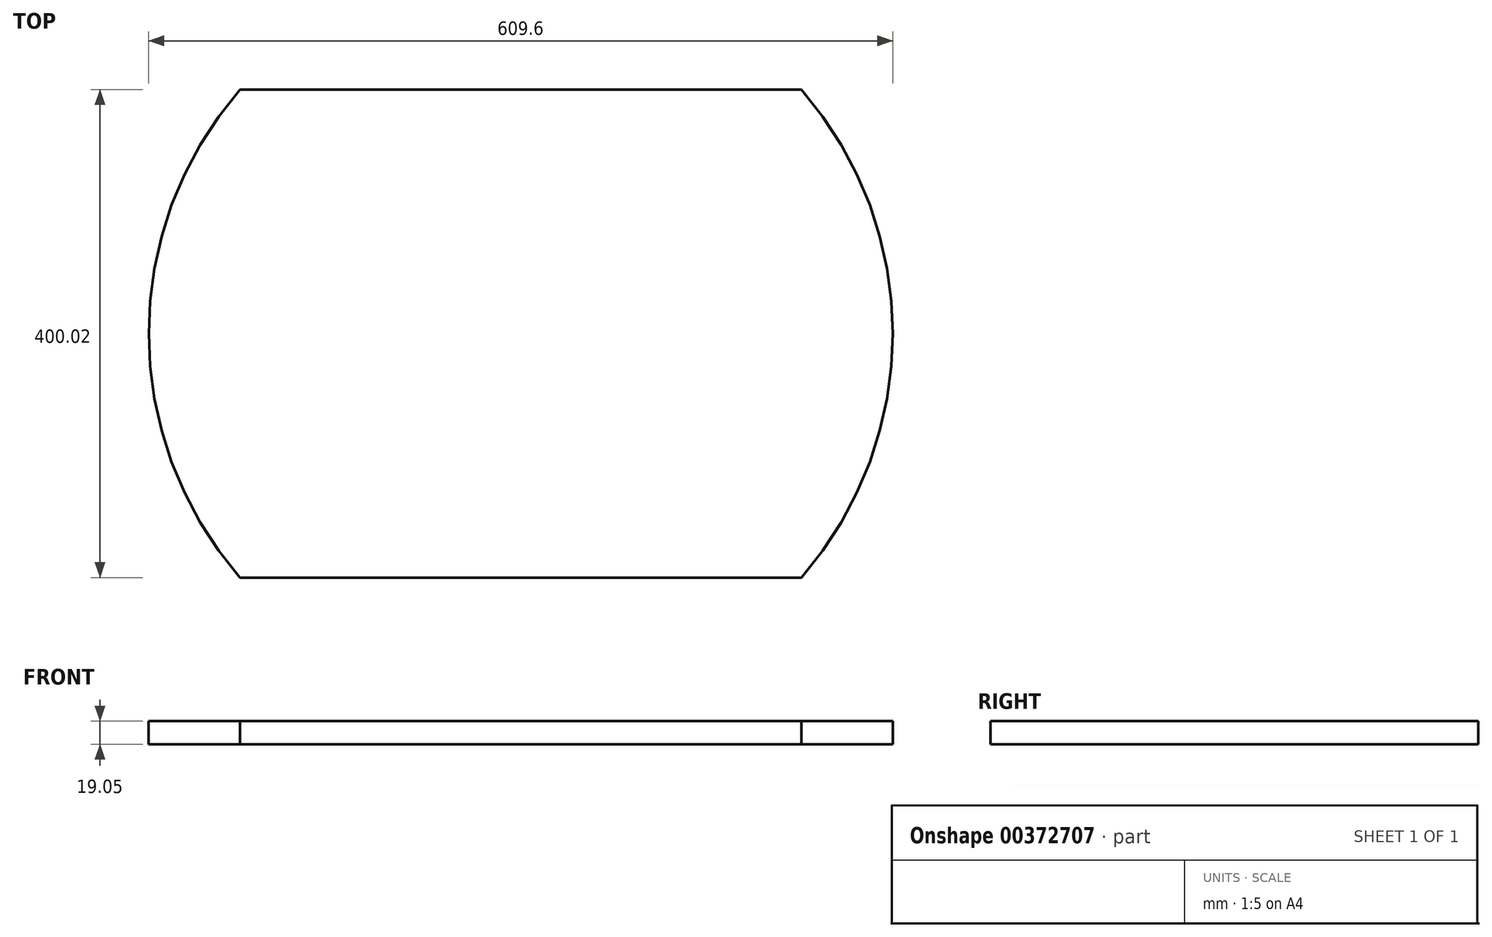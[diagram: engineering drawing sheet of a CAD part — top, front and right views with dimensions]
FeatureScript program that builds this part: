
annotation { "Feature Type Name" : "Feature", "Feature Type Description" : "" }
export const myFeature = defineFeature(function(context is Context, id is Id, definition is map)
    precondition{}
    {
        {
            var Q0;
            Q0=qCreatedBy(makeId("Top.planeOp"),FACE);
            var sketch = newSketch(context, id + "F0", { "sketchPlane" : qUnion([Q0])});
            skCircle(sketch, "E0", {"center": v(0, 0) * mm, "radius": 304.8 * mm});
            skSolve(sketch);
        }
        {
            var Q0;
            Q0 = qSketchRegion(id + "F0", true);
            extrude(context, id + "F1", {"entities" : qUnion([Q0]), "depth" : 19.05 * mm});
        }
        {
            var Q0;
            Q0=makeQuery(id+"F1.opExtrude","SWEPT_BODY",BODY,{"disambiguationData":[OSD([sQuery(id+"F0.wireOp",EDGE,"E0")])]});
            transform(context, id + "F2", {"entities" : qUnion([Q0]), "transformType" : TransformType.TRANSLATION_3D, "dx" : 0 * mm, "dy" : 0 * mm, "dz" : -515.62 * mm, "makeCopy" : true});
        }
        {
            var Q0;
            Q0=makeQuery(id+"F2.opPattern","COPY",BODY,{"derivedFrom":makeQuery(id+"F1.opExtrude","SWEPT_BODY",BODY,{"disambiguationData":[OSD([sQuery(id+"F0.wireOp",EDGE,"E0")])]}),"instanceName":"1"});
            deleteBodies(context, id + "F3", {"entities" : qUnion([Q0])});
        }
        {
            var Q0;
            Q0=makeQuery(id+"F1.opExtrude","CAP_FACE",FACE,{"disambiguationData":[OSD([sQuery(id+"F0.wireOp",EDGE,"E0")])],"isStart":false});
            var sketch = newSketch(context, id + "F4", { "sketchPlane" : qUnion([Q0])});
            skLineSegment(sketch, "E1.bottom", {"start": v(-332.42, -200) * mm, "end": v(319.37, -200) * mm});
            skLineSegment(sketch, "E1.top", {"start": v(-332.42, -360.57) * mm, "end": v(319.37, -360.57) * mm});
            skLineSegment(sketch, "E1.left", {"start": v(-332.42, -200) * mm, "end": v(-332.42, -360.57) * mm});
            skLineSegment(sketch, "E1.right", {"start": v(319.37, -200) * mm, "end": v(319.37, -360.57) * mm});
            skLineSegment(sketch, "E2", {"start": v(0, 0) * mm, "end": v(384.21, 0) * mm, "construction": true});
            skLineSegment(sketch, "E3.MirrorCS", {"start": v(-332.42, 200) * mm, "end": v(319.37, 200) * mm});
            skLineSegment(sketch, "E4.MirrorCS", {"start": v(-332.42, 360.57) * mm, "end": v(319.37, 360.57) * mm});
            skLineSegment(sketch, "E5.MirrorCS", {"start": v(319.37, 200) * mm, "end": v(319.37, 360.57) * mm});
            skLineSegment(sketch, "E6.MirrorCS", {"start": v(-332.42, 200) * mm, "end": v(-332.42, 360.57) * mm});
            skSolve(sketch);
        }
        {
            var Q0;
            Q0 = qSketchRegion(id + "F4", true);
            extrude(context, id + "F5", {"entities" : qUnion([Q0]), "operationType" : NewBodyOperationType.REMOVE, "oppositeDirection" : true, "depth" : 25.4 * mm});
        }
    });
